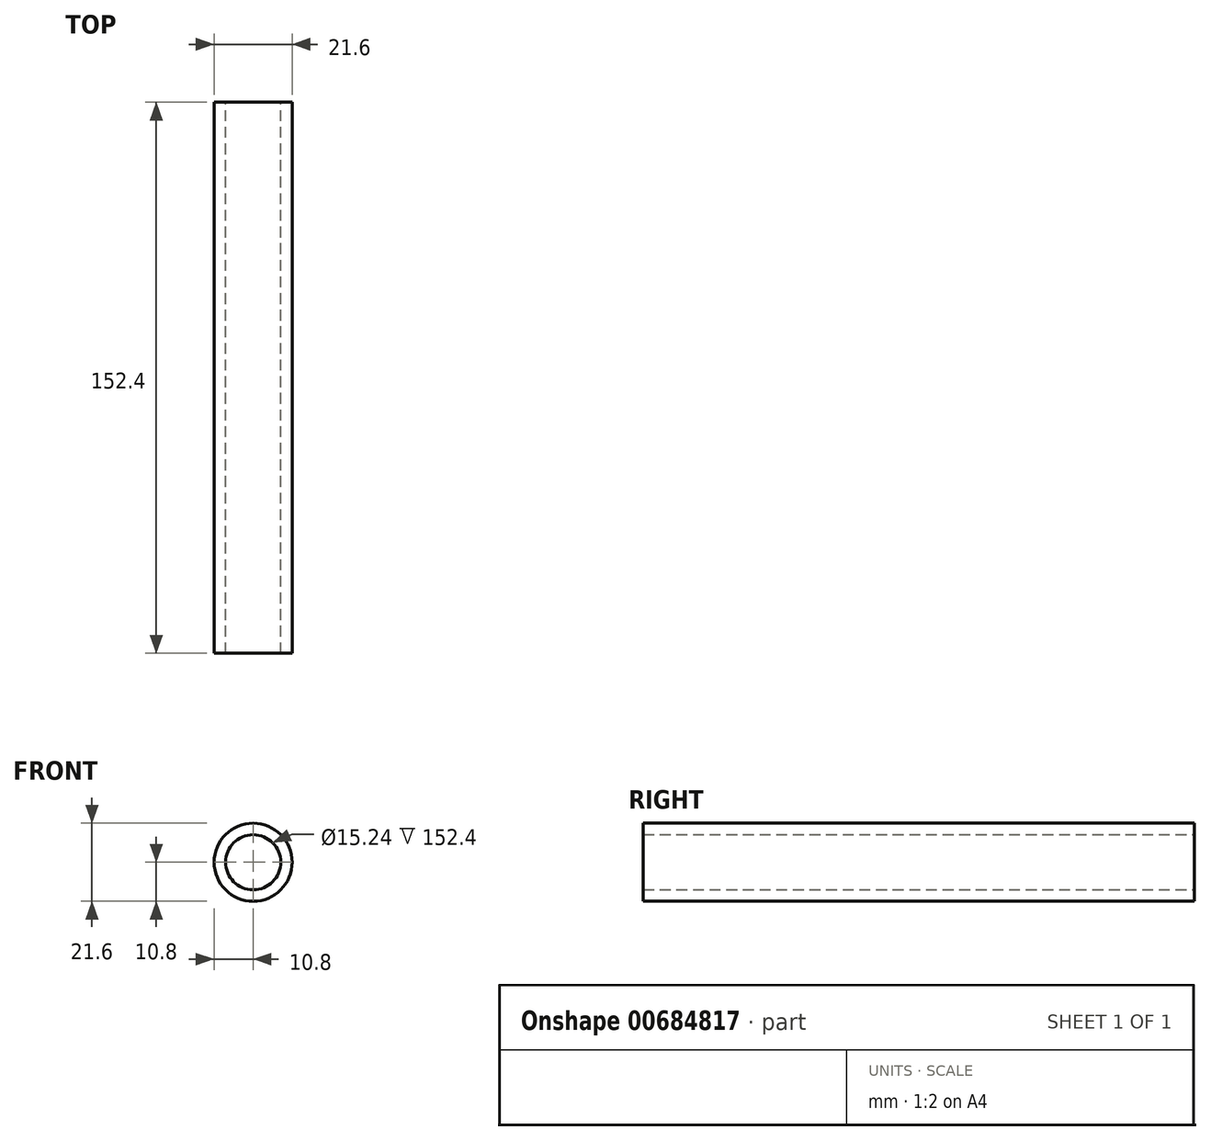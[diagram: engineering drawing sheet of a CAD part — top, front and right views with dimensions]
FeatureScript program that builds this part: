
annotation { "Feature Type Name" : "Feature", "Feature Type Description" : "" }
export const myFeature = defineFeature(function(context is Context, id is Id, definition is map)
    precondition{}
    {
        {
            var Q0;
            Q0=qCreatedBy(makeId("Front.planeOp"),FACE);
            var sketch = newSketch(context, id + "F0", { "sketchPlane" : qUnion([Q0])});
            skCircle(sketch, "E0", {"center": v(0, 0) * mm, "radius": 10.8 * mm});
            skCircle(sketch, "E1", {"center": v(0, 0) * mm, "radius": 7.62 * mm});
            skSolve(sketch);
        }
        {
            var Q0;
            Q0=makeQuery(id+"F0.imprint","IMPRINT",FACE,{"disambiguationData":[TD([[makeQuery(id+"F0.imprint","IMPRINT",EDGE,{"derivedFrom":sQuery(id+"F0.wireOp",EDGE,"E0")}),1.0]])]});
            extrude(context, id + "F1", {"entities" : qUnion([Q0]), "depth" : 152.4 * mm, "offsetDistance" : 25.4 * mm});
        }
    });
